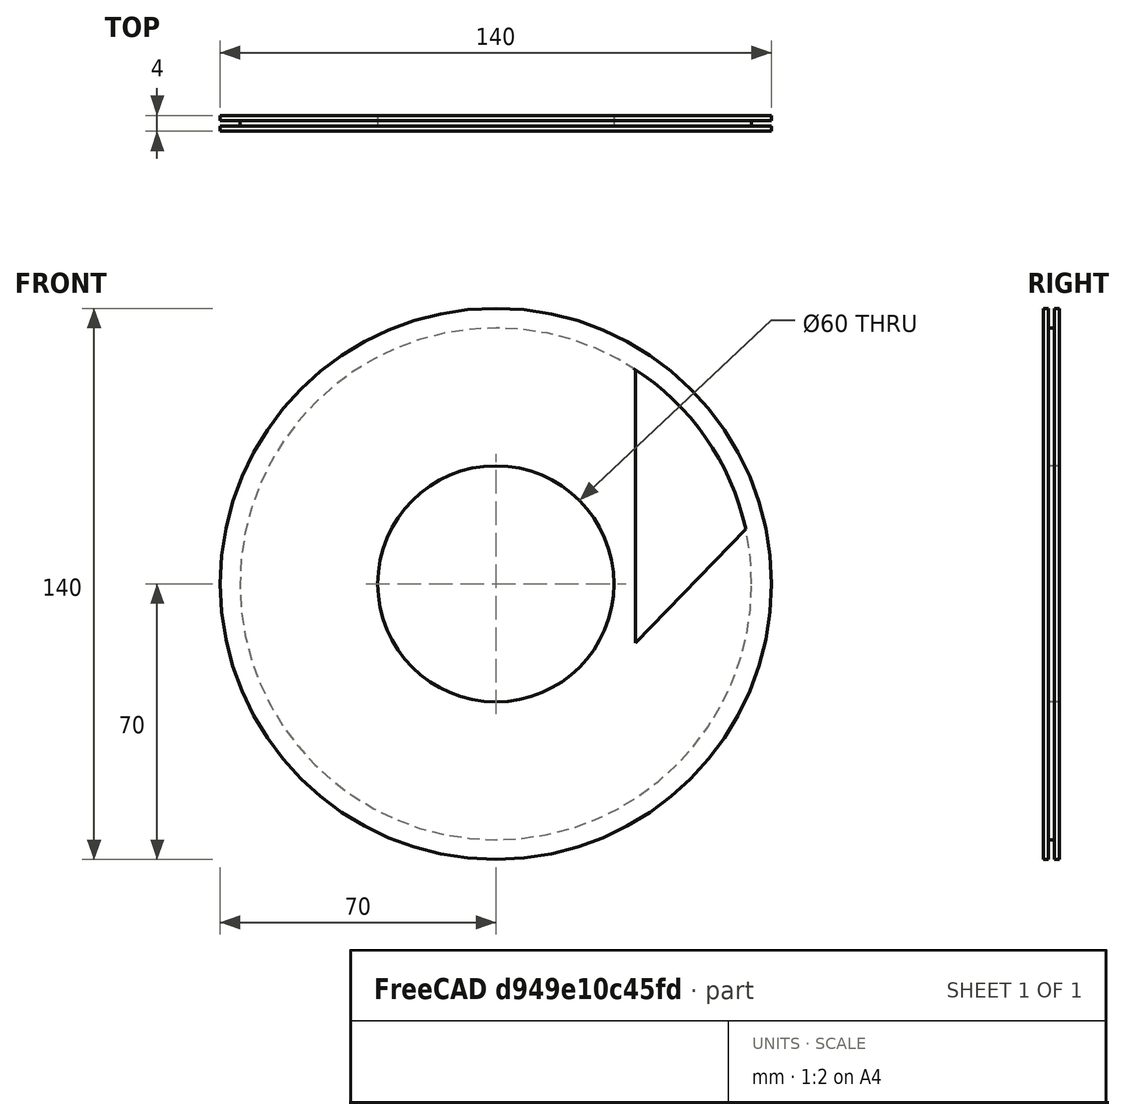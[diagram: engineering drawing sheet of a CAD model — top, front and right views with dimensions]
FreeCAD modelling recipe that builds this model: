
FCSTD DOCUMENT
Label: logo
objects: Sketcher::SketchObject×2, Part::Feature×2, Part::Revolution×1
note: 5 computed .brp shape members not serialized (recipe doc carries the construction recipe); baked Part::Feature solids carry a one-line shape summary decoded from their .brp

FEATURE [Sketcher::SketchObject] Sketch
  sketch-geometry (8):
    g0: LineSegment StartX=30 StartY=0 StartZ=0 EndX=70 EndY=0 EndZ=0
    g1: LineSegment StartX=70 StartY=0 StartZ=0 EndX=70 EndY=1.25 EndZ=0
    g2: LineSegment StartX=70 StartY=1.25 StartZ=0 EndX=65 EndY=1.25 EndZ=0
    g3: LineSegment StartX=65 StartY=1.25 StartZ=0 EndX=65 EndY=2.75 EndZ=0
    g4: LineSegment StartX=65 StartY=2.75 StartZ=0 EndX=70 EndY=2.75 EndZ=0
    g5: LineSegment StartX=70 StartY=2.75 StartZ=0 EndX=70 EndY=4 EndZ=0
    g6: LineSegment StartX=70 StartY=4 StartZ=0 EndX=30 EndY=4 EndZ=0
    g7: LineSegment StartX=30 StartY=4 StartZ=0 EndX=30 EndY=0 EndZ=0
  constraints (24):
    c: Horizontal(g0)
    c: Coincident(g1,g0)
    c: Coincident(g2,g1)
    c: Horizontal(g2)
    c: Vertical(g3)
    c: Coincident(g4,g3)
    c: Horizontal(g4)
    c: Coincident(g6,g5)
    c: Horizontal(g6)
    c: Coincident(g7,g6)
    c: Coincident(g7,g0)
    c: Distance(g0) = 40
    c: Distance(g-1,g0) = 30
    c: DistanceY(g-1,g0) = 0
    c: Distance(g1) = 1.25
    c: Coincident(g2,g3)
    c: Distance(g3) = 1.5
    c: Coincident(g5,g4)
    c: Parallel(g5,g1)
    c: Parallel(g5,g7)
    c: Perpendicular(g7,g0)
    c: Distance(g7) = 4
    c: Distance(g6) = 40
    c: Distance(g4) = 5
FEATURE [Part::Revolution] Revolve
  Angle = 360
  Axis = (0,1,0)
  Base = (0,0,0)
  Source = -> Sketch
FEATURE [Sketcher::SketchObject] Sketch001
  Placement = pos=(0,0,0) rot=(1,0,0;1.5708rad)
  Support = -> Revolve [Face1]
  sketch-geometry (5):
    g0: GeomPoint [constr] X=29.6204 Y=-18.6449 Z=0
    g1: GeomPoint [constr] X=65 Y=0 Z=0
    g2: LineSegment StartX=29.6204 StartY=-18.6449 StartZ=0 EndX=48.7231 EndY=43.024 EndZ=0
    g3: LineSegment StartX=65 StartY=0 StartZ=0 EndX=29.6204 EndY=-18.6449 EndZ=0
    g4: ArcOfCircle CenterX=0 CenterY=0 CenterZ=0 NormalX=0 NormalY=0 NormalZ=1 Radius=65 StartAngle=0 EndAngle=0.72336
  constraints (11):
    c: PointOnObject(g1,g-1)
    c: Coincident(g2,g0)
    c: Coincident(g3,g1)
    c: Coincident(g3,g0)
    c: Angle(g3,g2) = 0.785398
    c: Distance(g-1,g0) = 35
    c: Distance(g2,g1) = 46
    c: Coincident(g4,g-1)
    c: Coincident(g4,g2)
    c: Coincident(g4,g1)
    c: Distance(g-1,g2) = 65
FEATURE [Part::Feature] Face
  shape: bbox 28.47 x 2e-07 x 69.74 mm, 1 faces, 0 solids (baked)
FEATURE [Part::Feature] Face001
  shape: bbox 28.47 x 2e-07 x 69.74 mm, 1 faces, 0 solids (baked)
